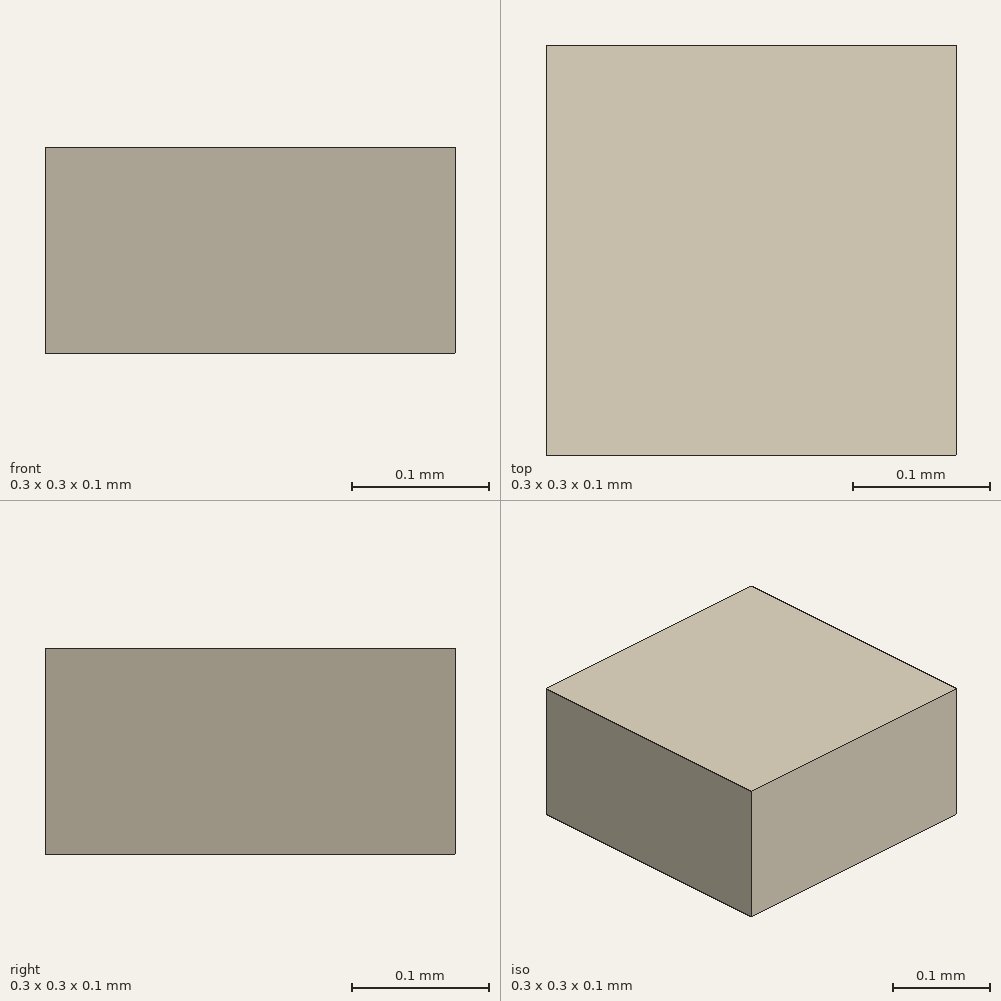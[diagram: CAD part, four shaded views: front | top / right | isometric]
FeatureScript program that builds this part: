
annotation { "Feature Type Name" : "Feature", "Feature Type Description" : "" }
export const myFeature = defineFeature(function(context is Context, id is Id, definition is map)
    precondition{}
    {
        {
            var Q0;
            Q0=qCreatedBy(makeId("Top.planeOp"),FACE);
            var sketch = newSketch(context, id + "F0", { "sketchPlane" : qUnion([Q0])});
            skLineSegment(sketch, "E0.bottom", {"start": v(1.03, 0) * mm, "end": v(1.33, 0) * mm});
            skLineSegment(sketch, "E0.top", {"start": v(1.03, -0.3) * mm, "end": v(1.33, -0.3) * mm});
            skLineSegment(sketch, "E0.left", {"start": v(1.03, 0) * mm, "end": v(1.03, -0.3) * mm});
            skLineSegment(sketch, "E0.right", {"start": v(1.33, 0) * mm, "end": v(1.33, -0.3) * mm});
            skSolve(sketch);
        }
        {
            var Q0;
            Q0 = qSketchRegion(id + "F0", true);
            extrude(context, id + "F1", {"entities" : qUnion([Q0]), "depth" : 0.15 * mm, "offsetDistance" : 25 * mm});
        }
    });
